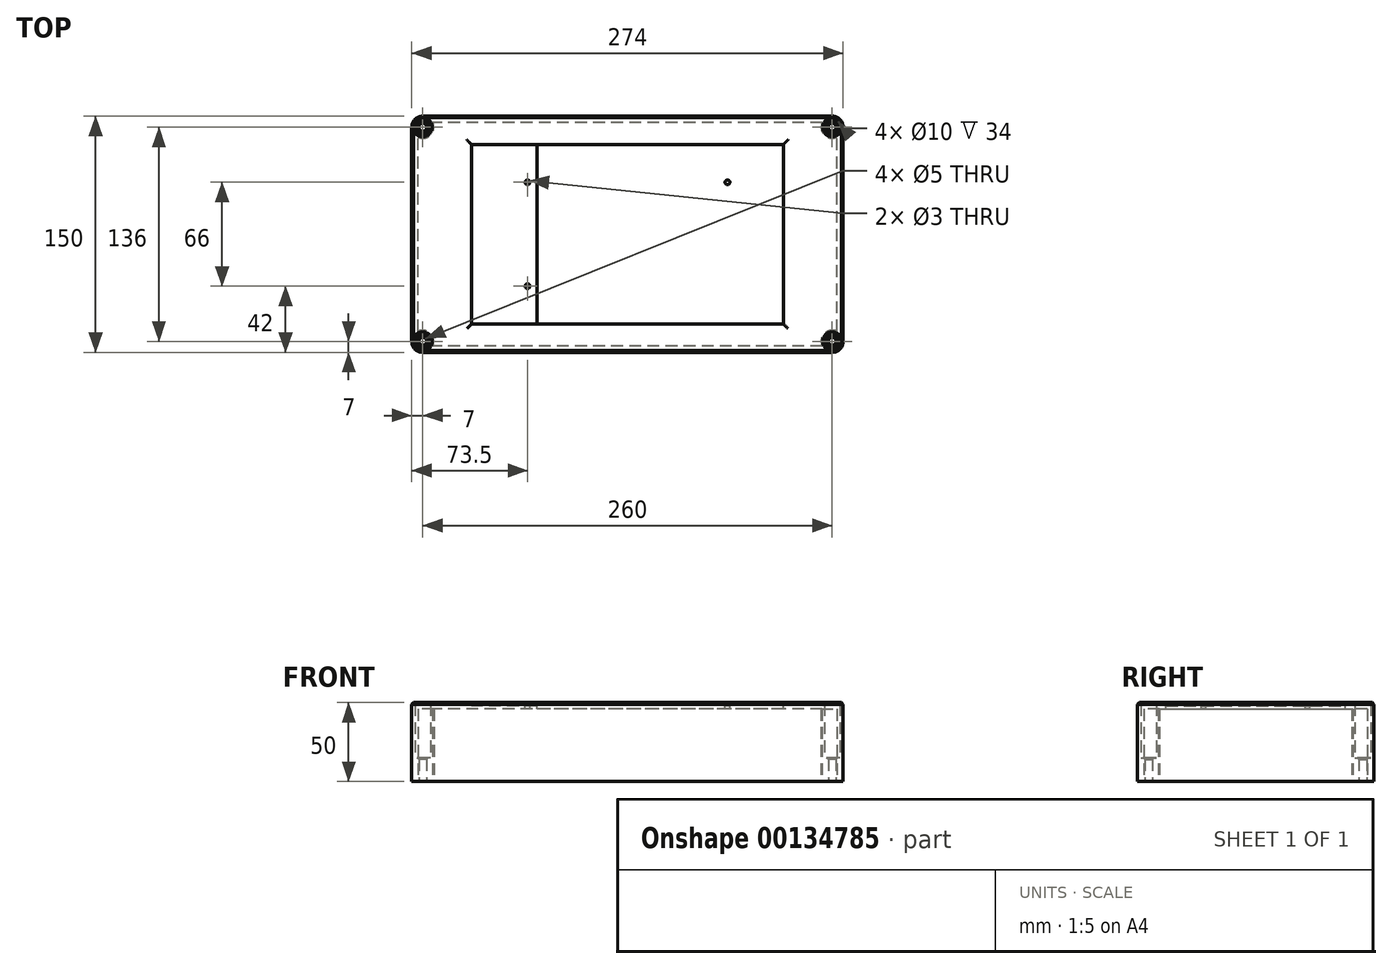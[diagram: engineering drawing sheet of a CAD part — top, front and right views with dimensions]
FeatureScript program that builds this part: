
annotation { "Feature Type Name" : "Feature", "Feature Type Description" : "" }
export const myFeature = defineFeature(function(context is Context, id is Id, definition is map)
    precondition{}
    {
        {
            var Q0;
            Q0=qCreatedBy(makeId("Top.planeOp"),FACE);
            var sketch = newSketch(context, id + "F0", { "sketchPlane" : qUnion([Q0])});
            skLineSegment(sketch, "E0.bottom", {"start": v(97, -55) * mm, "end": v(-97, -55) * mm, "construction": true});
            skLineSegment(sketch, "E0.top", {"start": v(97, 55) * mm, "end": v(-97, 55) * mm, "construction": true});
            skLineSegment(sketch, "E0.left", {"start": v(97, -55) * mm, "end": v(97, 55) * mm, "construction": true});
            skLineSegment(sketch, "E0.right", {"start": v(-97, -55) * mm, "end": v(-97, 55) * mm, "construction": true});
            skPoint(sketch, "E0.middle", {"position": v(0, 0) * mm});
            skLineSegment(sketch, "E1.bottom", {"start": v(137, -75) * mm, "end": v(-137, -75) * mm});
            skLineSegment(sketch, "E1.top", {"start": v(137, 75) * mm, "end": v(-137, 75) * mm});
            skLineSegment(sketch, "E1.left", {"start": v(137, -75) * mm, "end": v(137, 75) * mm});
            skLineSegment(sketch, "E1.right", {"start": v(-137, -75) * mm, "end": v(-137, 75) * mm});
            skLineSegment(sketch, "E2.0", {"start": v(133, 71) * mm, "end": v(-133, 71) * mm});
            skLineSegment(sketch, "E2.1", {"start": v(133, -71) * mm, "end": v(133, 71) * mm});
            skLineSegment(sketch, "E2.2", {"start": v(133, -71) * mm, "end": v(-133, -71) * mm});
            skLineSegment(sketch, "E2.3", {"start": v(-133, -71) * mm, "end": v(-133, 71) * mm});
            skCircle(sketch, "E3", {"center": v(-130, 68) * mm, "radius": 7 * mm});
            skLineSegment(sketch, "E4.0", {"start": v(130, 68) * mm, "end": v(-130, 68) * mm, "construction": true});
            skLineSegment(sketch, "E4.1", {"start": v(130, -68) * mm, "end": v(130, 68) * mm, "construction": true});
            skLineSegment(sketch, "E4.2", {"start": v(130, -68) * mm, "end": v(-130, -68) * mm, "construction": true});
            skLineSegment(sketch, "E4.3", {"start": v(-130, -68) * mm, "end": v(-130, 68) * mm, "construction": true});
            skCircle(sketch, "E5.MirrorC", {"center": v(130, 68) * mm, "radius": 7 * mm});
            skCircle(sketch, "E6.MirrorC", {"center": v(-130, -68) * mm, "radius": 7 * mm});
            skCircle(sketch, "E7.MirrorC", {"center": v(130, -68) * mm, "radius": 7 * mm});
            skCircle(sketch, "E8", {"center": v(-130, 68) * mm, "radius": 2.5 * mm});
            skCircle(sketch, "E9", {"center": v(-130, 68) * mm, "radius": 5 * mm});
            skCircle(sketch, "E10.MirrorC", {"center": v(130, 68) * mm, "radius": 5 * mm});
            skCircle(sketch, "E11.MirrorC", {"center": v(130, 68) * mm, "radius": 2.5 * mm});
            skCircle(sketch, "E12.MirrorC", {"center": v(-130, -68) * mm, "radius": 2.5 * mm});
            skCircle(sketch, "E13.MirrorC", {"center": v(-130, -68) * mm, "radius": 5 * mm});
            skCircle(sketch, "E14.MirrorC", {"center": v(130, -68) * mm, "radius": 2.5 * mm});
            skCircle(sketch, "E15.MirrorC", {"center": v(130, -68) * mm, "radius": 5 * mm});
            skSolve(sketch);
        }
        {
            var Q0;
            {var subQ0=sQuery(id+"F0.wireOp",EDGE,"E5.MirrorC");var subQ1=sQuery(id+"F0.wireOp",EDGE,"E1.top");var subQ2=makeQuery(id+"F0.imprint","INTERSECT",VERTEX,{"derivedFrom":[subQ1,subQ0]});Q0=makeQuery(id+"F0.imprint","IMPRINT",FACE,{"disambiguationData":[TD([[makeQuery(id+"F0.imprint","IMPRINT",EDGE,{"disambiguationData":[TD([[subQ2,-1.0]])],"derivedFrom":subQ1}),1.0]])]});}
            var Q1;
            {var subQ0=sQuery(id+"F0.wireOp",EDGE,"E6.MirrorC");var subQ1=sQuery(id+"F0.wireOp",EDGE,"E1.right");var subQ2=makeQuery(id+"F0.imprint","INTERSECT",VERTEX,{"derivedFrom":[subQ1,subQ0]});Q1=makeQuery(id+"F0.imprint","IMPRINT",FACE,{"disambiguationData":[TD([[makeQuery(id+"F0.imprint","IMPRINT",EDGE,{"disambiguationData":[TD([[subQ2,-1.0]])],"derivedFrom":subQ1}),-1.0]])]});}
            var Q2;
            {var subQ0=sQuery(id+"F0.wireOp",EDGE,"E7.MirrorC");var subQ1=sQuery(id+"F0.wireOp",EDGE,"E1.bottom");var subQ2=makeQuery(id+"F0.imprint","INTERSECT",VERTEX,{"derivedFrom":[subQ1,subQ0]});Q2=makeQuery(id+"F0.imprint","IMPRINT",FACE,{"disambiguationData":[TD([[makeQuery(id+"F0.imprint","IMPRINT",EDGE,{"disambiguationData":[TD([[subQ2,-1.0]])],"derivedFrom":subQ1}),-1.0]])]});}
            var Q3;
            {var subQ0=sQuery(id+"F0.wireOp",EDGE,"E7.MirrorC");var subQ1=sQuery(id+"F0.wireOp",EDGE,"E1.left");var subQ2=makeQuery(id+"F0.imprint","INTERSECT",VERTEX,{"derivedFrom":[subQ1,subQ0]});Q3=makeQuery(id+"F0.imprint","IMPRINT",FACE,{"disambiguationData":[TD([[makeQuery(id+"F0.imprint","IMPRINT",EDGE,{"disambiguationData":[TD([[subQ2,-1.0]])],"derivedFrom":subQ1}),1.0]])]});}
            var Q4;
            {var subQ0=sQuery(id+"F0.wireOp",EDGE,"E3");var subQ3=sQuery(id+"F0.wireOp",EDGE,"E2.0");var subQ4=makeQuery(id+"F0.imprint","INTERSECT",VERTEX,{"derivedFrom":[subQ3,subQ0]});Q4=makeQuery(id+"F0.imprint","IMPRINT",FACE,{"disambiguationData":[TD([[makeQuery(id+"F0.imprint","IMPRINT",EDGE,{"disambiguationData":[TD([[subQ4,-1.0]])],"derivedFrom":subQ3}),-1.0]])]});}
            var Q5;
            {var subQ0=sQuery(id+"F0.wireOp",EDGE,"E3");var subQ1=sQuery(id+"F0.wireOp",EDGE,"E2.0");var subQ2=makeQuery(id+"F0.imprint","INTERSECT",VERTEX,{"derivedFrom":[subQ1,subQ0]});Q5=makeQuery(id+"F0.imprint","IMPRINT",FACE,{"disambiguationData":[TD([[makeQuery(id+"F0.imprint","IMPRINT",EDGE,{"disambiguationData":[TD([[subQ2,-1.0]])],"derivedFrom":subQ1}),1.0]])]});}
            var Q6;
            {var subQ0=sQuery(id+"F0.wireOp",EDGE,"E6.MirrorC");var subQ3=sQuery(id+"F0.wireOp",EDGE,"E2.2");var subQ4=makeQuery(id+"F0.imprint","INTERSECT",VERTEX,{"derivedFrom":[subQ3,subQ0]});Q6=makeQuery(id+"F0.imprint","IMPRINT",FACE,{"disambiguationData":[TD([[makeQuery(id+"F0.imprint","IMPRINT",EDGE,{"disambiguationData":[TD([[subQ4,-1.0]])],"derivedFrom":subQ3}),1.0]])]});}
            var Q7;
            {var subQ0=sQuery(id+"F0.wireOp",EDGE,"E6.MirrorC");var subQ1=sQuery(id+"F0.wireOp",EDGE,"E2.2");var subQ2=makeQuery(id+"F0.imprint","INTERSECT",VERTEX,{"derivedFrom":[subQ1,subQ0]});Q7=makeQuery(id+"F0.imprint","IMPRINT",FACE,{"disambiguationData":[TD([[makeQuery(id+"F0.imprint","IMPRINT",EDGE,{"disambiguationData":[TD([[subQ2,-1.0]])],"derivedFrom":subQ1}),-1.0]])]});}
            var Q8;
            {var subQ3=sQuery(id+"F0.wireOp",EDGE,"E15.MirrorC");var subQ7=sQuery(id+"F0.wireOp",EDGE,"E2.1");var subQ8=makeQuery(id+"F0.imprint","INTERSECT",VERTEX,{"derivedFrom":[subQ7,subQ3]});Q8=makeQuery(id+"F0.imprint","IMPRINT",FACE,{"disambiguationData":[TD([[makeQuery(id+"F0.imprint","IMPRINT",EDGE,{"disambiguationData":[TD([[subQ8,-1.0]])],"derivedFrom":subQ7}),-1.0]])]});}
            var Q9;
            {var subQ0=sQuery(id+"F0.wireOp",EDGE,"E15.MirrorC");var subQ1=sQuery(id+"F0.wireOp",EDGE,"E2.1");var subQ2=makeQuery(id+"F0.imprint","INTERSECT",VERTEX,{"derivedFrom":[subQ1,subQ0]});Q9=makeQuery(id+"F0.imprint","IMPRINT",FACE,{"disambiguationData":[TD([[makeQuery(id+"F0.imprint","IMPRINT",EDGE,{"disambiguationData":[TD([[subQ2,-1.0]])],"derivedFrom":subQ1}),1.0]])]});}
            var Q10;
            {var subQ5=sQuery(id+"F0.wireOp",EDGE,"E10.MirrorC");var subQ7=sQuery(id+"F0.wireOp",EDGE,"E2.0");var subQ9=makeQuery(id+"F0.imprint","INTERSECT",VERTEX,{"derivedFrom":[subQ7,subQ5]});Q10=makeQuery(id+"F0.imprint","IMPRINT",FACE,{"disambiguationData":[TD([[makeQuery(id+"F0.imprint","IMPRINT",EDGE,{"disambiguationData":[TD([[subQ9,-1.0]])],"derivedFrom":subQ7}),-1.0]])]});}
            var Q11;
            {var subQ0=sQuery(id+"F0.wireOp",EDGE,"E10.MirrorC");var subQ1=sQuery(id+"F0.wireOp",EDGE,"E2.0");var subQ2=makeQuery(id+"F0.imprint","INTERSECT",VERTEX,{"derivedFrom":[subQ1,subQ0]});Q11=makeQuery(id+"F0.imprint","IMPRINT",FACE,{"disambiguationData":[TD([[makeQuery(id+"F0.imprint","IMPRINT",EDGE,{"disambiguationData":[TD([[subQ2,-1.0]])],"derivedFrom":subQ1}),1.0]])]});}
            extrude(context, id + "F1", {"entities" : qUnion([Q0, Q1, Q2, Q3, Q4, Q5, Q6, Q7, Q8, Q9, Q10, Q11]), "depth" : 50 * mm});
        }
        {
            var Q0;
            {var subQ0=sQuery(id+"F0.wireOp",EDGE,"E9");var subQ1=sQuery(id+"F0.wireOp",EDGE,"E2.0");var subQ2=makeQuery(id+"F0.imprint","INTERSECT",VERTEX,{"derivedFrom":[subQ1,subQ0]});Q0=makeQuery(id+"F0.imprint","IMPRINT",FACE,{"disambiguationData":[TD([[makeQuery(id+"F0.imprint","IMPRINT",EDGE,{"disambiguationData":[TD([[subQ2,-1.0]])],"derivedFrom":subQ1}),-1.0]])]});}
            var Q1;
            {var subQ0=sQuery(id+"F0.wireOp",EDGE,"E9");var subQ1=sQuery(id+"F0.wireOp",EDGE,"E2.0");var subQ2=makeQuery(id+"F0.imprint","INTERSECT",VERTEX,{"derivedFrom":[subQ1,subQ0]});Q1=makeQuery(id+"F0.imprint","IMPRINT",FACE,{"disambiguationData":[TD([[makeQuery(id+"F0.imprint","IMPRINT",EDGE,{"disambiguationData":[TD([[subQ2,-1.0]])],"derivedFrom":subQ1}),1.0]])]});}
            var Q2;
            {var subQ0=sQuery(id+"F0.wireOp",EDGE,"E13.MirrorC");var subQ1=sQuery(id+"F0.wireOp",EDGE,"E2.2");var subQ2=makeQuery(id+"F0.imprint","INTERSECT",VERTEX,{"derivedFrom":[subQ1,subQ0]});Q2=makeQuery(id+"F0.imprint","IMPRINT",FACE,{"disambiguationData":[TD([[makeQuery(id+"F0.imprint","IMPRINT",EDGE,{"disambiguationData":[TD([[subQ2,-1.0]])],"derivedFrom":subQ1}),-1.0]])]});}
            var Q3;
            {var subQ0=sQuery(id+"F0.wireOp",EDGE,"E13.MirrorC");var subQ1=sQuery(id+"F0.wireOp",EDGE,"E2.2");var subQ2=makeQuery(id+"F0.imprint","INTERSECT",VERTEX,{"derivedFrom":[subQ1,subQ0]});Q3=makeQuery(id+"F0.imprint","IMPRINT",FACE,{"disambiguationData":[TD([[makeQuery(id+"F0.imprint","IMPRINT",EDGE,{"disambiguationData":[TD([[subQ2,-1.0]])],"derivedFrom":subQ1}),1.0]])]});}
            var Q4;
            {var subQ0=sQuery(id+"F0.wireOp",EDGE,"E14.MirrorC");var subQ1=sQuery(id+"F0.wireOp",EDGE,"E2.1");var subQ2=makeQuery(id+"F0.imprint","INTERSECT",VERTEX,{"derivedFrom":[subQ1,subQ0]});Q4=makeQuery(id+"F0.imprint","IMPRINT",FACE,{"disambiguationData":[TD([[makeQuery(id+"F0.imprint","IMPRINT",EDGE,{"disambiguationData":[TD([[subQ2,-1.0]])],"derivedFrom":subQ1}),1.0]])]});}
            var Q5;
            {var subQ0=sQuery(id+"F0.wireOp",EDGE,"E14.MirrorC");var subQ1=sQuery(id+"F0.wireOp",EDGE,"E2.1");var subQ2=makeQuery(id+"F0.imprint","INTERSECT",VERTEX,{"derivedFrom":[subQ1,subQ0]});Q5=makeQuery(id+"F0.imprint","IMPRINT",FACE,{"disambiguationData":[TD([[makeQuery(id+"F0.imprint","IMPRINT",EDGE,{"disambiguationData":[TD([[subQ2,-1.0]])],"derivedFrom":subQ1}),-1.0]])]});}
            var Q6;
            {var subQ0=sQuery(id+"F0.wireOp",EDGE,"E11.MirrorC");var subQ1=sQuery(id+"F0.wireOp",EDGE,"E2.0");var subQ2=makeQuery(id+"F0.imprint","INTERSECT",VERTEX,{"derivedFrom":[subQ1,subQ0]});Q6=makeQuery(id+"F0.imprint","IMPRINT",FACE,{"disambiguationData":[TD([[makeQuery(id+"F0.imprint","IMPRINT",EDGE,{"disambiguationData":[TD([[subQ2,-1.0]])],"derivedFrom":subQ1}),1.0]])]});}
            var Q7;
            {var subQ0=sQuery(id+"F0.wireOp",EDGE,"E11.MirrorC");var subQ1=sQuery(id+"F0.wireOp",EDGE,"E2.0");var subQ2=makeQuery(id+"F0.imprint","INTERSECT",VERTEX,{"derivedFrom":[subQ1,subQ0]});Q7=makeQuery(id+"F0.imprint","IMPRINT",FACE,{"disambiguationData":[TD([[makeQuery(id+"F0.imprint","IMPRINT",EDGE,{"disambiguationData":[TD([[subQ2,-1.0]])],"derivedFrom":subQ1}),-1.0]])]});}
            extrude(context, id + "F2", {"entities" : qUnion([Q0, Q1, Q2, Q3, Q4, Q5, Q6, Q7]), "operationType" : NewBodyOperationType.ADD, "depth" : 15 * mm});
        }
        {
            var Q0;
            Q0=makeQuery(id+"F1.opExtrude","CAP_FACE",FACE,{"disambiguationData":[OSD([sQuery(id+"F0.wireOp",EDGE,"E1.bottom"),sQuery(id+"F0.wireOp",EDGE,"E1.top"),sQuery(id+"F0.wireOp",EDGE,"E1.left"),sQuery(id+"F0.wireOp",EDGE,"E1.right"),sQuery(id+"F0.wireOp",EDGE,"E2.0"),sQuery(id+"F0.wireOp",EDGE,"E2.1"),sQuery(id+"F0.wireOp",EDGE,"E2.2"),sQuery(id+"F0.wireOp",EDGE,"E2.3"),sQuery(id+"F0.wireOp",EDGE,"E3"),sQuery(id+"F0.wireOp",EDGE,"E5.MirrorC"),sQuery(id+"F0.wireOp",EDGE,"E6.MirrorC"),sQuery(id+"F0.wireOp",EDGE,"E7.MirrorC"),sQuery(id+"F0.wireOp",EDGE,"E9"),sQuery(id+"F0.wireOp",EDGE,"E10.MirrorC"),sQuery(id+"F0.wireOp",EDGE,"E13.MirrorC"),sQuery(id+"F0.wireOp",EDGE,"E15.MirrorC")])],"isStart":false});
            var sketch = newSketch(context, id + "F3", { "sketchPlane" : qUnion([Q0])});
            skLineSegment(sketch, "E16.bottom", {"start": v(97, -55) * mm, "end": v(-97, -55) * mm, "construction": true});
            skLineSegment(sketch, "E16.top", {"start": v(97, 55) * mm, "end": v(-97, 55) * mm, "construction": true});
            skLineSegment(sketch, "E16.left", {"start": v(97, -55) * mm, "end": v(97, 55) * mm, "construction": true});
            skLineSegment(sketch, "E16.right", {"start": v(-97, -55) * mm, "end": v(-97, 55) * mm, "construction": true});
            skLineSegment(sketch, "E17.0", {"start": v(99, 57) * mm, "end": v(-99, 57) * mm});
            skLineSegment(sketch, "E17.1", {"start": v(99, -57) * mm, "end": v(99, 57) * mm});
            skLineSegment(sketch, "E17.2", {"start": v(99, -57) * mm, "end": v(-99, -57) * mm});
            skLineSegment(sketch, "E17.3", {"start": v(-99, -57) * mm, "end": v(-99, 57) * mm});
            skSolve(sketch);
        }
        {
            var Q0;
            Q0=makeQuery(id+"F3.imprint","IMPRINT",FACE,{"disambiguationData":[TD([[makeQuery(id+"F3.imprint","IMPRINT",EDGE,{"derivedFrom":sQuery(id+"F3.wireOp",EDGE,"E17.0")}),-1.0]])]});
            extrude(context, id + "F4", {"entities" : qUnion([Q0]), "operationType" : NewBodyOperationType.ADD, "oppositeDirection" : true, "depth" : 4 * mm});
        }
        {
            var Q0;
            {var subQ3=sQuery(id+"F0.wireOp",EDGE,"E1.bottom");Q0=makeQuery(id+"F3.imprint","IMPRINT",FACE,{"disambiguationData":[TD([[makeQuery(id+"F3.imprint","IMPRINT",EDGE,{"derivedFrom":makeQuery(id+"F1.opExtrude","CAP_EDGE",EDGE,{"disambiguationData":[OSD([subQ3])],"isStart":false})}),-1.0]])]});}
            var sketch = newSketch(context, id + "F5", { "sketchPlane" : qUnion([Q0])});
            skLineSegment(sketch, "E18.bottom", {"start": v(63.5, -33) * mm, "end": v(-63.5, -33) * mm, "construction": true});
            skLineSegment(sketch, "E18.top", {"start": v(63.5, 33) * mm, "end": v(-63.5, 33) * mm, "construction": true});
            skLineSegment(sketch, "E18.left", {"start": v(63.5, -33) * mm, "end": v(63.5, 33) * mm, "construction": true});
            skLineSegment(sketch, "E18.right", {"start": v(-63.5, -33) * mm, "end": v(-63.5, 33) * mm, "construction": true});
            skPoint(sketch, "E18.middle", {"position": v(0, 0) * mm});
            skCircle(sketch, "E19", {"center": v(-63.5, 33) * mm, "radius": 1.5 * mm});
            skCircle(sketch, "E20.MirrorC", {"center": v(63.5, 33) * mm, "radius": 1.5 * mm});
            skCircle(sketch, "E21.MirrorC", {"center": v(-63.5, -33) * mm, "radius": 1.5 * mm});
            skCircle(sketch, "E22.MirrorC", {"center": v(63.5, -33) * mm, "radius": 1.5 * mm});
            skLineSegment(sketch, "E23", {"start": v(-57.5, 57) * mm, "end": v(-57.5, -57) * mm});
            skLineSegment(sketch, "E24.MirrorCS", {"start": v(57.5, 57) * mm, "end": v(57.5, -57) * mm});
            skLineSegment(sketch, "E25.bottom", {"start": v(99, -57) * mm, "end": v(-99, -57) * mm});
            skLineSegment(sketch, "E25.top", {"start": v(99, 57) * mm, "end": v(-99, 57) * mm});
            skLineSegment(sketch, "E25.left", {"start": v(99, -57) * mm, "end": v(99, 57) * mm});
            skLineSegment(sketch, "E25.right", {"start": v(-99, -57) * mm, "end": v(-99, 57) * mm});
            skSolve(sketch);
        }
        {
            var Q0;
            Q0=makeQuery(id+"F5.imprint","IMPRINT",FACE,{"disambiguationData":[TD([[makeQuery(id+"F5.imprint","IMPRINT",EDGE,{"derivedFrom":sQuery(id+"F5.wireOp",EDGE,"E19")}),-1.0]])]});
            var Q1;
            Q1=makeQuery(id+"F5.imprint","IMPRINT",FACE,{"disambiguationData":[TD([[makeQuery(id+"F5.imprint","IMPRINT",EDGE,{"derivedFrom":sQuery(id+"F5.wireOp",EDGE,"E20.MirrorC")}),1.0]])]});
            extrude(context, id + "F6", {"entities" : qUnion([Q0, Q1]), "operationType" : NewBodyOperationType.ADD, "oppositeDirection" : true, "depth" : 4 * mm, "hasSecondDirection" : true, "secondDirectionOppositeDirection" : true, "secondDirectionDepth" : 2 * mm});
        }
        {
            var Q0;
            Q0=makeQuery(id+"F1.opExtrude","CAP_EDGE",EDGE,{"disambiguationData":[OSD([sQuery(id+"F0.wireOp",EDGE,"E9")])],"isStart":false});
            var Q1;
            Q1=makeQuery(id+"F1.opExtrude","CAP_EDGE",EDGE,{"disambiguationData":[OSD([sQuery(id+"F0.wireOp",EDGE,"E13.MirrorC")])],"isStart":false});
            var Q2;
            Q2=makeQuery(id+"F1.opExtrude","CAP_EDGE",EDGE,{"disambiguationData":[OSD([sQuery(id+"F0.wireOp",EDGE,"E10.MirrorC")])],"isStart":false});
            var Q3;
            Q3=makeQuery(id+"F1.opExtrude","CAP_EDGE",EDGE,{"disambiguationData":[OSD([sQuery(id+"F0.wireOp",EDGE,"E15.MirrorC")])],"isStart":false});
            chamfer(context, id + "F7", {"entities" : qUnion([Q0, Q1, Q2, Q3]), "width" : 1 * mm, "tangentPropagation" : true});
        }
        {
            var Q0;
            Q0=makeQuery(id+"F1.opExtrude","CAP_EDGE",EDGE,{"disambiguationData":[OSD([sQuery(id+"F0.wireOp",EDGE,"E1.top")])],"isStart":false});
            chamfer(context, id + "F8", {"entities" : qUnion([Q0]), "width" : 1 * mm, "tangentPropagation" : true});
        }
        {
            var Q0;
            Q0=makeQuery(id+"F2.opExtrude","CAP_EDGE",EDGE,{"disambiguationData":[OSD([sQuery(id+"F0.wireOp",EDGE,"E8")])],"isStart":false});
            var Q1;
            Q1=makeQuery(id+"F2.opExtrude","CAP_EDGE",EDGE,{"disambiguationData":[OSD([sQuery(id+"F0.wireOp",EDGE,"E11.MirrorC")])],"isStart":false});
            var Q2;
            Q2=makeQuery(id+"F2.opExtrude","CAP_EDGE",EDGE,{"disambiguationData":[OSD([sQuery(id+"F0.wireOp",EDGE,"E14.MirrorC")])],"isStart":false});
            var Q3;
            Q3=makeQuery(id+"F2.opExtrude","CAP_EDGE",EDGE,{"disambiguationData":[OSD([sQuery(id+"F0.wireOp",EDGE,"E12.MirrorC")])],"isStart":false});
            chamfer(context, id + "F9", {"entities" : qUnion([Q0, Q1, Q2, Q3]), "width" : 1 * mm, "tangentPropagation" : true});
        }
        {
            var Q0;
            Q0=makeQuery(id+"F4.opExtrude","CAP_EDGE",EDGE,{"disambiguationData":[OSD([sQuery(id+"F3.wireOp",EDGE,"E17.0")])],"isStart":true});
            var Q1;
            Q1=makeQuery(id+"F4.opExtrude","CAP_EDGE",EDGE,{"disambiguationData":[OSD([sQuery(id+"F3.wireOp",EDGE,"E17.3")])],"isStart":true});
            var Q2;
            Q2=makeQuery(id+"F4.opExtrude","CAP_EDGE",EDGE,{"disambiguationData":[OSD([sQuery(id+"F3.wireOp",EDGE,"E17.2")])],"isStart":true});
            var Q3;
            Q3=makeQuery(id+"F4.opExtrude","CAP_EDGE",EDGE,{"disambiguationData":[OSD([sQuery(id+"F3.wireOp",EDGE,"E17.1")])],"isStart":true});
            chamfer(context, id + "F10", {"entities" : qUnion([Q0, Q1, Q2, Q3]), "width" : 1 * mm, "tangentPropagation" : true});
        }
        {
            var Q0;
            {var subQ0=sQuery(id+"F3.wireOp",EDGE,"E17.0");var subQ1=sQuery(id+"F0.wireOp",EDGE,"E7.MirrorC");var subQ2=sQuery(id+"F0.wireOp",EDGE,"E6.MirrorC");var subQ3=sQuery(id+"F0.wireOp",EDGE,"E5.MirrorC");var subQ4=sQuery(id+"F0.wireOp",EDGE,"E3");var subQ5=sQuery(id+"F0.wireOp",EDGE,"E2.3");var subQ6=sQuery(id+"F0.wireOp",EDGE,"E2.2");var subQ7=sQuery(id+"F0.wireOp",EDGE,"E2.1");var subQ8=sQuery(id+"F0.wireOp",EDGE,"E2.0");Q0=makeQuery(id+"F10.opChamfer","BLEND_EDGE",EDGE,{"blendedFrom":[makeQuery(id+"F4.opExtrude","CAP_EDGE",EDGE,{"disambiguationData":[OSD([subQ0])],"isStart":true}),makeQuery(id+"F4.boolean.opBoolean","MERGE",FACE,{"derivedFrom":[makeQuery(id+"F1.opExtrude","CAP_FACE",FACE,{"disambiguationData":[OSD([sQuery(id+"F0.wireOp",EDGE,"E1.bottom"),sQuery(id+"F0.wireOp",EDGE,"E1.top"),sQuery(id+"F0.wireOp",EDGE,"E1.left"),sQuery(id+"F0.wireOp",EDGE,"E1.right"),subQ8,subQ7,subQ6,subQ5,subQ4,subQ3,subQ2,subQ1,sQuery(id+"F0.wireOp",EDGE,"E9"),sQuery(id+"F0.wireOp",EDGE,"E10.MirrorC"),sQuery(id+"F0.wireOp",EDGE,"E13.MirrorC"),sQuery(id+"F0.wireOp",EDGE,"E15.MirrorC")])],"isStart":false}),makeQuery(id+"F4.opExtrude","CAP_FACE",FACE,{"disambiguationData":[OSD([subQ8,subQ7,subQ6,subQ5,subQ4,subQ3,subQ2,subQ1,subQ0,sQuery(id+"F3.wireOp",EDGE,"E17.1"),sQuery(id+"F3.wireOp",EDGE,"E17.2"),sQuery(id+"F3.wireOp",EDGE,"E17.3")])],"isStart":true})]})],"blendedInto":[makeQuery(id+"F4.boolean.opBoolean","MERGE",FACE,{"derivedFrom":[makeQuery(id+"F1.opExtrude","CAP_FACE",FACE,{"disambiguationData":[OSD([sQuery(id+"F0.wireOp",EDGE,"E1.bottom"),sQuery(id+"F0.wireOp",EDGE,"E1.top"),sQuery(id+"F0.wireOp",EDGE,"E1.left"),sQuery(id+"F0.wireOp",EDGE,"E1.right"),subQ8,subQ7,subQ6,subQ5,subQ4,subQ3,subQ2,subQ1,sQuery(id+"F0.wireOp",EDGE,"E9"),sQuery(id+"F0.wireOp",EDGE,"E10.MirrorC"),sQuery(id+"F0.wireOp",EDGE,"E13.MirrorC"),sQuery(id+"F0.wireOp",EDGE,"E15.MirrorC")])],"isStart":false}),makeQuery(id+"F4.opExtrude","CAP_FACE",FACE,{"disambiguationData":[OSD([subQ8,subQ7,subQ6,subQ5,subQ4,subQ3,subQ2,subQ1,subQ0,sQuery(id+"F3.wireOp",EDGE,"E17.1"),sQuery(id+"F3.wireOp",EDGE,"E17.2"),sQuery(id+"F3.wireOp",EDGE,"E17.3")])],"isStart":true})]})]});}
            var Q1;
            {var subQ0=sQuery(id+"F3.wireOp",EDGE,"E17.3");var subQ1=sQuery(id+"F0.wireOp",EDGE,"E7.MirrorC");var subQ2=sQuery(id+"F0.wireOp",EDGE,"E6.MirrorC");var subQ3=sQuery(id+"F0.wireOp",EDGE,"E5.MirrorC");var subQ4=sQuery(id+"F0.wireOp",EDGE,"E3");var subQ5=sQuery(id+"F0.wireOp",EDGE,"E2.3");var subQ6=sQuery(id+"F0.wireOp",EDGE,"E2.2");var subQ7=sQuery(id+"F0.wireOp",EDGE,"E2.1");var subQ8=sQuery(id+"F0.wireOp",EDGE,"E2.0");Q1=makeQuery(id+"F10.opChamfer","BLEND_EDGE",EDGE,{"blendedFrom":[makeQuery(id+"F4.opExtrude","CAP_EDGE",EDGE,{"disambiguationData":[OSD([subQ0])],"isStart":true}),makeQuery(id+"F4.boolean.opBoolean","MERGE",FACE,{"derivedFrom":[makeQuery(id+"F1.opExtrude","CAP_FACE",FACE,{"disambiguationData":[OSD([sQuery(id+"F0.wireOp",EDGE,"E1.bottom"),sQuery(id+"F0.wireOp",EDGE,"E1.top"),sQuery(id+"F0.wireOp",EDGE,"E1.left"),sQuery(id+"F0.wireOp",EDGE,"E1.right"),subQ8,subQ7,subQ6,subQ5,subQ4,subQ3,subQ2,subQ1,sQuery(id+"F0.wireOp",EDGE,"E9"),sQuery(id+"F0.wireOp",EDGE,"E10.MirrorC"),sQuery(id+"F0.wireOp",EDGE,"E13.MirrorC"),sQuery(id+"F0.wireOp",EDGE,"E15.MirrorC")])],"isStart":false}),makeQuery(id+"F4.opExtrude","CAP_FACE",FACE,{"disambiguationData":[OSD([subQ8,subQ7,subQ6,subQ5,subQ4,subQ3,subQ2,subQ1,sQuery(id+"F3.wireOp",EDGE,"E17.0"),sQuery(id+"F3.wireOp",EDGE,"E17.1"),sQuery(id+"F3.wireOp",EDGE,"E17.2"),subQ0])],"isStart":true})]})],"blendedInto":[makeQuery(id+"F4.boolean.opBoolean","MERGE",FACE,{"derivedFrom":[makeQuery(id+"F1.opExtrude","CAP_FACE",FACE,{"disambiguationData":[OSD([sQuery(id+"F0.wireOp",EDGE,"E1.bottom"),sQuery(id+"F0.wireOp",EDGE,"E1.top"),sQuery(id+"F0.wireOp",EDGE,"E1.left"),sQuery(id+"F0.wireOp",EDGE,"E1.right"),subQ8,subQ7,subQ6,subQ5,subQ4,subQ3,subQ2,subQ1,sQuery(id+"F0.wireOp",EDGE,"E9"),sQuery(id+"F0.wireOp",EDGE,"E10.MirrorC"),sQuery(id+"F0.wireOp",EDGE,"E13.MirrorC"),sQuery(id+"F0.wireOp",EDGE,"E15.MirrorC")])],"isStart":false}),makeQuery(id+"F4.opExtrude","CAP_FACE",FACE,{"disambiguationData":[OSD([subQ8,subQ7,subQ6,subQ5,subQ4,subQ3,subQ2,subQ1,sQuery(id+"F3.wireOp",EDGE,"E17.0"),sQuery(id+"F3.wireOp",EDGE,"E17.1"),sQuery(id+"F3.wireOp",EDGE,"E17.2"),subQ0])],"isStart":true})]})]});}
            var Q2;
            {var subQ0=sQuery(id+"F3.wireOp",EDGE,"E17.2");var subQ1=sQuery(id+"F0.wireOp",EDGE,"E7.MirrorC");var subQ2=sQuery(id+"F0.wireOp",EDGE,"E6.MirrorC");var subQ3=sQuery(id+"F0.wireOp",EDGE,"E5.MirrorC");var subQ4=sQuery(id+"F0.wireOp",EDGE,"E3");var subQ5=sQuery(id+"F0.wireOp",EDGE,"E2.3");var subQ6=sQuery(id+"F0.wireOp",EDGE,"E2.2");var subQ7=sQuery(id+"F0.wireOp",EDGE,"E2.1");var subQ8=sQuery(id+"F0.wireOp",EDGE,"E2.0");Q2=makeQuery(id+"F10.opChamfer","BLEND_EDGE",EDGE,{"blendedFrom":[makeQuery(id+"F4.opExtrude","CAP_EDGE",EDGE,{"disambiguationData":[OSD([subQ0])],"isStart":true}),makeQuery(id+"F4.boolean.opBoolean","MERGE",FACE,{"derivedFrom":[makeQuery(id+"F1.opExtrude","CAP_FACE",FACE,{"disambiguationData":[OSD([sQuery(id+"F0.wireOp",EDGE,"E1.bottom"),sQuery(id+"F0.wireOp",EDGE,"E1.top"),sQuery(id+"F0.wireOp",EDGE,"E1.left"),sQuery(id+"F0.wireOp",EDGE,"E1.right"),subQ8,subQ7,subQ6,subQ5,subQ4,subQ3,subQ2,subQ1,sQuery(id+"F0.wireOp",EDGE,"E9"),sQuery(id+"F0.wireOp",EDGE,"E10.MirrorC"),sQuery(id+"F0.wireOp",EDGE,"E13.MirrorC"),sQuery(id+"F0.wireOp",EDGE,"E15.MirrorC")])],"isStart":false}),makeQuery(id+"F4.opExtrude","CAP_FACE",FACE,{"disambiguationData":[OSD([subQ8,subQ7,subQ6,subQ5,subQ4,subQ3,subQ2,subQ1,sQuery(id+"F3.wireOp",EDGE,"E17.0"),sQuery(id+"F3.wireOp",EDGE,"E17.1"),subQ0,sQuery(id+"F3.wireOp",EDGE,"E17.3")])],"isStart":true})]})],"blendedInto":[makeQuery(id+"F4.boolean.opBoolean","MERGE",FACE,{"derivedFrom":[makeQuery(id+"F1.opExtrude","CAP_FACE",FACE,{"disambiguationData":[OSD([sQuery(id+"F0.wireOp",EDGE,"E1.bottom"),sQuery(id+"F0.wireOp",EDGE,"E1.top"),sQuery(id+"F0.wireOp",EDGE,"E1.left"),sQuery(id+"F0.wireOp",EDGE,"E1.right"),subQ8,subQ7,subQ6,subQ5,subQ4,subQ3,subQ2,subQ1,sQuery(id+"F0.wireOp",EDGE,"E9"),sQuery(id+"F0.wireOp",EDGE,"E10.MirrorC"),sQuery(id+"F0.wireOp",EDGE,"E13.MirrorC"),sQuery(id+"F0.wireOp",EDGE,"E15.MirrorC")])],"isStart":false}),makeQuery(id+"F4.opExtrude","CAP_FACE",FACE,{"disambiguationData":[OSD([subQ8,subQ7,subQ6,subQ5,subQ4,subQ3,subQ2,subQ1,sQuery(id+"F3.wireOp",EDGE,"E17.0"),sQuery(id+"F3.wireOp",EDGE,"E17.1"),subQ0,sQuery(id+"F3.wireOp",EDGE,"E17.3")])],"isStart":true})]})]});}
            var Q3;
            {var subQ0=sQuery(id+"F3.wireOp",EDGE,"E17.1");var subQ1=sQuery(id+"F0.wireOp",EDGE,"E7.MirrorC");var subQ2=sQuery(id+"F0.wireOp",EDGE,"E6.MirrorC");var subQ3=sQuery(id+"F0.wireOp",EDGE,"E5.MirrorC");var subQ4=sQuery(id+"F0.wireOp",EDGE,"E3");var subQ5=sQuery(id+"F0.wireOp",EDGE,"E2.3");var subQ6=sQuery(id+"F0.wireOp",EDGE,"E2.2");var subQ7=sQuery(id+"F0.wireOp",EDGE,"E2.1");var subQ8=sQuery(id+"F0.wireOp",EDGE,"E2.0");Q3=makeQuery(id+"F10.opChamfer","BLEND_EDGE",EDGE,{"blendedFrom":[makeQuery(id+"F4.opExtrude","CAP_EDGE",EDGE,{"disambiguationData":[OSD([subQ0])],"isStart":true}),makeQuery(id+"F4.boolean.opBoolean","MERGE",FACE,{"derivedFrom":[makeQuery(id+"F1.opExtrude","CAP_FACE",FACE,{"disambiguationData":[OSD([sQuery(id+"F0.wireOp",EDGE,"E1.bottom"),sQuery(id+"F0.wireOp",EDGE,"E1.top"),sQuery(id+"F0.wireOp",EDGE,"E1.left"),sQuery(id+"F0.wireOp",EDGE,"E1.right"),subQ8,subQ7,subQ6,subQ5,subQ4,subQ3,subQ2,subQ1,sQuery(id+"F0.wireOp",EDGE,"E9"),sQuery(id+"F0.wireOp",EDGE,"E10.MirrorC"),sQuery(id+"F0.wireOp",EDGE,"E13.MirrorC"),sQuery(id+"F0.wireOp",EDGE,"E15.MirrorC")])],"isStart":false}),makeQuery(id+"F4.opExtrude","CAP_FACE",FACE,{"disambiguationData":[OSD([subQ8,subQ7,subQ6,subQ5,subQ4,subQ3,subQ2,subQ1,sQuery(id+"F3.wireOp",EDGE,"E17.0"),subQ0,sQuery(id+"F3.wireOp",EDGE,"E17.2"),sQuery(id+"F3.wireOp",EDGE,"E17.3")])],"isStart":true})]})],"blendedInto":[makeQuery(id+"F4.boolean.opBoolean","MERGE",FACE,{"derivedFrom":[makeQuery(id+"F1.opExtrude","CAP_FACE",FACE,{"disambiguationData":[OSD([sQuery(id+"F0.wireOp",EDGE,"E1.bottom"),sQuery(id+"F0.wireOp",EDGE,"E1.top"),sQuery(id+"F0.wireOp",EDGE,"E1.left"),sQuery(id+"F0.wireOp",EDGE,"E1.right"),subQ8,subQ7,subQ6,subQ5,subQ4,subQ3,subQ2,subQ1,sQuery(id+"F0.wireOp",EDGE,"E9"),sQuery(id+"F0.wireOp",EDGE,"E10.MirrorC"),sQuery(id+"F0.wireOp",EDGE,"E13.MirrorC"),sQuery(id+"F0.wireOp",EDGE,"E15.MirrorC")])],"isStart":false}),makeQuery(id+"F4.opExtrude","CAP_FACE",FACE,{"disambiguationData":[OSD([subQ8,subQ7,subQ6,subQ5,subQ4,subQ3,subQ2,subQ1,sQuery(id+"F3.wireOp",EDGE,"E17.0"),subQ0,sQuery(id+"F3.wireOp",EDGE,"E17.2"),sQuery(id+"F3.wireOp",EDGE,"E17.3")])],"isStart":true})]})]});}
            fillet(context, id + "F11", {"entities" : qUnion([Q0, Q1, Q2, Q3]), "radius" : 5 * mm, "tangentPropagation" : true, "allowEdgeOverflow" : false});
        }
    });
